# Revit family: Gira_215400
name_source: partatom
category: Elektroinstallationen
revit_build: Autodesk Revit 2017 (Build: 20160225_1515(x64)
units: mm (PartAtom-declared; Revit-internal decimal feet)

## family parameters
Basisbauteil = Fläche
Beim Laden mit Abzugskörper schneiden = Nein
Bemaßung runder Anschluss = Durchmesser verwenden
Beschriftungsausrichtung beibehalten = Nein
Gemeinsam genutzt = Nein
Raumberechnungspunkt = Nein
Teiletyp = Normal

## types (1)
- Jal.aktor 4f DC 24 V Hand KNX REG
    Andere Bussysteme = ohne
    Anzahl der Ausgänge = 0
    Anzahl der Eingänge = 1
    Anzahl der binären Eingänge = 0
    BIM = https://media.stage.bim.site 8f.rfa
    BIMSITE_PRODUCT_ID = 1aa0b8a5083b45cd90cee0a2b70e4dc2af69c131
    Bemessungsstrom = 0 A
    Beschreibung = KNX Jalousieaktor 4fach DC 24 V mit Handbetätigung  REG plus Jalousieaktoren mit integrierter Busankopplung, Handbetätigung und Statusanzeige für jeden Ausgang. Zum Ansteuern von elektrisch betriebenen Jalousien, Rollläden, Markisen, Lüftungsklappen oder ähnlichen Behängen.  Merkmale:  Behangposition direkt ansteuerbar.  Lamellenstellung direkt ansteuerbar.  Verhalten bei Busspannungsausfall und -wiederkehr einstellbar.  Separat parametrierbare Fahrzeiten mit Fahrzeitverlängerung für Fahrten in die obere Endlage.  Zentrale Ansteuerung aller Jalousieausgänge möglich.  Rückmeldung der Behangposition oder der Lamellenposition.  Rückmeldungen lassen sich nach Busspannungswiederkehr verzögern.  Zuordnungen auf bis zu fünf verschiedene Sicherheitsfunktionen (drei Windalarme, ein Regenalarm, ein Frostalarm), wahlweise mit zyklischer Überwachung.  Zwangsstellungsfunktion für jeden Jalousieausgang realisierbar.  Einbeziehung in Szenen möglich, max. acht interne Szenen je Kanal sind parametrierbar.  Speicherfunktion für Lichtszenen.  Sonnenschutzfunktion mit festen und variablen Behang- oder Lamellenpositionen aktivierbar.  Erweiterter Sonnenschutz mit umfangreichen Steuerfunktionen.  Einbindung in Temperatur-Management des Gebäudes möglich.  Sperren einzelner Ausgänge per Hand oder Bus.  Aktive oder passive (Objekt auslesbar) zyklische Rückmeldefunktionen.  Baustellenbetrieb: Ausgänge manuell bedienbar ohne Busspannung nur mit der Betriebsspannung.  Für Kleinspannung DC 12 bis 48 V.  Unabhängige Ansteuerung der vier Jalousieausgänge.  Hinweise :  Montage auf DIN-Hutschiene.
    Blindleistung = Nein
    Breite in Teilungseinheiten = 4
    Busspannung pufferbar = Nein
    Bussystem Funkbus = Nein
    Bussystem KNX = Ja
    Bussystem KNX-Funk = Nein
    Bussystem LON = Nein
    Bussystem Powernet = Nein
    Datenblatt = https://media.stage.bim.site
    Datenblatt 1 = https://media.stage.bim.site
    Funktion Schalten = Nein
    GTIN = 4010337082248
    Geeignet für C-Last = Nein
    HAN = 215400
    Handschaltung = Nein
    HeinzeBIM = https://www.heinze.de
    Hersteller = Gira
    Kosten = 0 $
    LED ansteuern = Nein
    Max. Anzahl der Jalousieausgänge = 4
    Max. Anzahl der Schaltausgänge = 0
    Max. Ausgangsstrom = 0 A
    Max. Schaltleistung [Voltampere] = 0
    Max. Schaltstrom = 0 A
    Mit Busankopplung = Ja
    Mit LED-Anzeige = Nein
    Modulare Erweiterungsmöglichkeit = Nein
    Montageart = REG
    Produktseite = https://media.stage.bim.site
    Schaltstrom ohmsch = 0 A
    Schutzart (IP) = IP20
    Stellgröße schaltend = Nein
    Stellgröße stetig = Nein
    Stromart = DC
    Tarifumschaltung = Nein
    Typname = Jal.aktor 4f DC 24 V Hand KNX REG
    URL = https://www.gira.de
    Ventilschutzfunktion = Nein
    Verschiedene Phasen anschließbar = Nein
    Vor Ort-/Handbedienung = Ja
    Vorgabe-Ansicht = 1219 mm
    Zulassung nach PTB = Nein

## geometry (parser evidence)
native form markers: Sweep x3
no freeform markers — native parametric forms only
